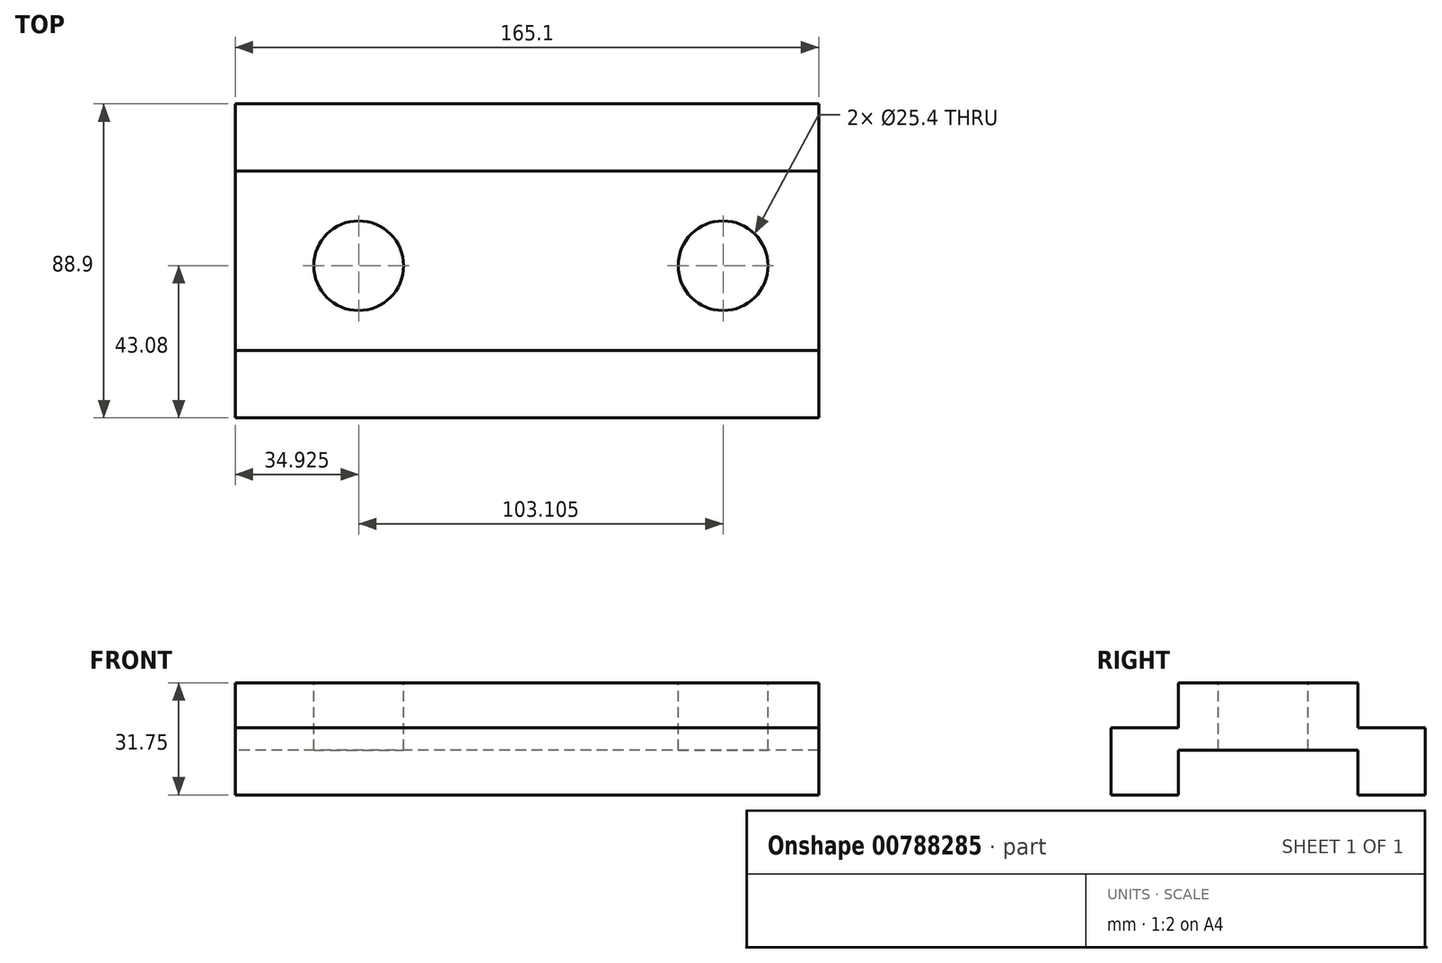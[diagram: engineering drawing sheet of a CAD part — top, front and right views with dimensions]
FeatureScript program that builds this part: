
annotation { "Feature Type Name" : "Feature", "Feature Type Description" : "" }
export const myFeature = defineFeature(function(context is Context, id is Id, definition is map)
    precondition{}
    {
        {
            var Q0;
            Q0=qCreatedBy(makeId("Right.planeOp"),FACE);
            var sketch = newSketch(context, id + "F0", { "sketchPlane" : qUnion([Q0])});
            skLineSegment(sketch, "E0", {"start": v(0, 0) * mm, "end": v(0, 19.05) * mm});
            skLineSegment(sketch, "E1", {"start": v(0, 0) * mm, "end": v(9.22, 0) * mm});
            skLineSegment(sketch, "E2", {"start": v(0, 19.05) * mm, "end": v(19.05, 19.05) * mm});
            skLineSegment(sketch, "E3", {"start": v(19.05, 19.05) * mm, "end": v(19.05, 31.75) * mm});
            skLineSegment(sketch, "E4", {"start": v(19.05, 31.75) * mm, "end": v(69.85, 31.75) * mm});
            skLineSegment(sketch, "E5", {"start": v(69.85, 31.75) * mm, "end": v(69.85, 19.05) * mm});
            skLineSegment(sketch, "E6", {"start": v(69.85, 19.05) * mm, "end": v(88.9, 19.05) * mm});
            skLineSegment(sketch, "E7", {"start": v(88.9, 19.05) * mm, "end": v(88.9, 0) * mm});
            skLineSegment(sketch, "E8", {"start": v(88.9, 0) * mm, "end": v(69.85, 0) * mm});
            skLineSegment(sketch, "E9", {"start": v(69.85, 0) * mm, "end": v(69.85, 12.7) * mm});
            skLineSegment(sketch, "E10", {"start": v(69.85, 12.7) * mm, "end": v(19.05, 12.7) * mm});
            skLineSegment(sketch, "E11", {"start": v(19.05, 12.7) * mm, "end": v(19.05, 0) * mm});
            skPoint(sketch, "E11.endSnap0", {"position": v(4.61, 0) * mm});
            skLineSegment(sketch, "E12", {"start": v(19.05, 0) * mm, "end": v(9.22, 0) * mm});
            skSolve(sketch);
        }
        {
            var Q0;
            Q0 = qSketchRegion(id + "F0", true);
            extrude(context, id + "F1", {"entities" : qUnion([Q0]), "depth" : 165.1 * mm, "offsetDistance" : 25.4 * mm});
        }
        {
            var Q0;
            Q0=makeQuery(id+"F1.opExtrude","SWEPT_FACE",FACE,{"disambiguationData":[OSD([sQuery(id+"F0.wireOp",EDGE,"E4")])]});
            var sketch = newSketch(context, id + "F2", { "sketchPlane" : qUnion([Q0])});
            skLineSegment(sketch, "E13", {"start": v(0, 44.45) * mm, "end": v(41.28, 44.45) * mm, "construction": true});
            skLineSegment(sketch, "E14", {"start": v(41.28, 44.45) * mm, "end": v(72.56, 44.45) * mm, "construction": true});
            skSolve(sketch);
        }
        {
            var Q0;
            {var subQ0=sQuery(id+"F0.wireOp",EDGE,"E4");Q0=makeQuery(id+"F2.imprint","IMPRINT",FACE,{"disambiguationData":[TD([[makeQuery(id+"F2.imprint","IMPRINT",EDGE,{"derivedFrom":makeQuery(id+"F1.opExtrude","CAP_EDGE",EDGE,{"disambiguationData":[OSD([subQ0])],"isStart":true})}),-1.0]])]});}
            var sketch = newSketch(context, id + "F3", { "sketchPlane" : qUnion([Q0])});
            skLineSegment(sketch, "E15", {"start": v(0, 43.08) * mm, "end": v(34.93, 43.08) * mm, "construction": true});
            skLineSegment(sketch, "E16", {"start": v(34.93, 43.08) * mm, "end": v(138.03, 43.08) * mm, "construction": true});
            skCircle(sketch, "E17", {"center": v(34.93, 43.08) * mm, "radius": 12.7 * mm});
            skCircle(sketch, "E18", {"center": v(138.03, 43.08) * mm, "radius": 12.7 * mm});
            skSolve(sketch);
        }
        {
            var Q0;
            Q0=makeQuery(id+"F3.imprint","IMPRINT",FACE,{"disambiguationData":[TD([[makeQuery(id+"F3.imprint","IMPRINT",EDGE,{"derivedFrom":sQuery(id+"F3.wireOp",EDGE,"E17")}),1.0]])]});
            var Q1;
            Q1=makeQuery(id+"F3.imprint","IMPRINT",FACE,{"disambiguationData":[TD([[makeQuery(id+"F3.imprint","IMPRINT",EDGE,{"derivedFrom":sQuery(id+"F3.wireOp",EDGE,"E18")}),1.0]])]});
            extrude(context, id + "F4", {"entities" : qUnion([Q0, Q1]), "operationType" : NewBodyOperationType.REMOVE, "endBound" : BoundingType.UP_TO_NEXT, "oppositeDirection" : true, "depth" : 25.4 * mm, "offsetDistance" : 25.4 * mm});
        }
    });
